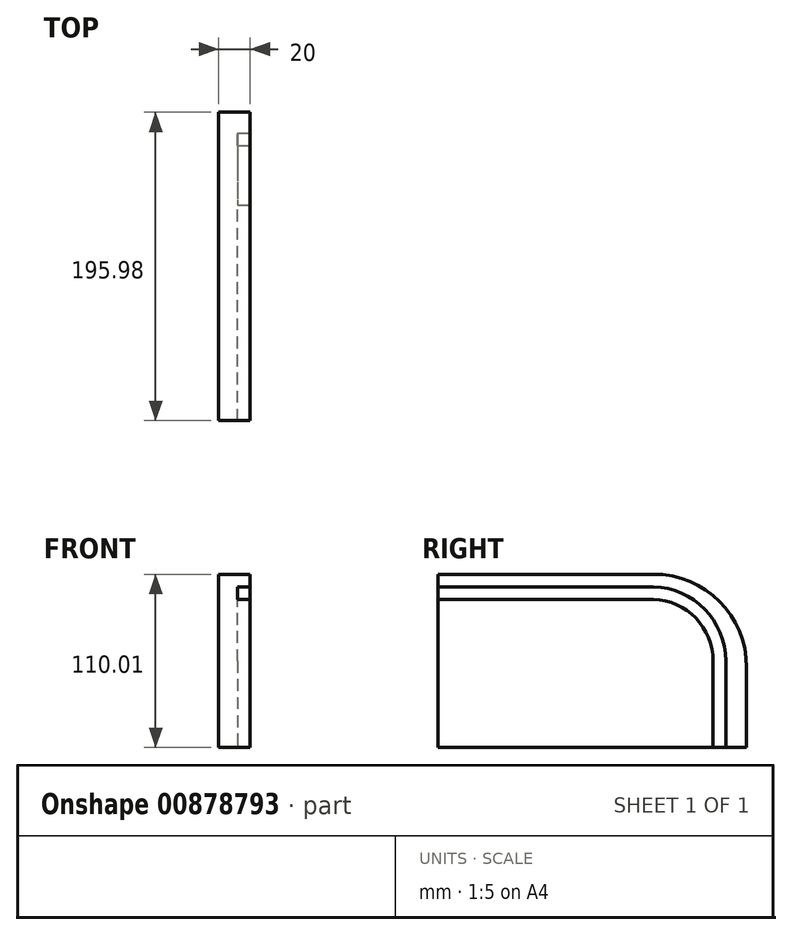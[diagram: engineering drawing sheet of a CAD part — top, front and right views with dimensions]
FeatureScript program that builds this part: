
annotation { "Feature Type Name" : "Feature", "Feature Type Description" : "" }
export const myFeature = defineFeature(function(context is Context, id is Id, definition is map)
    precondition{}
    {
        {
            var Q0;
            Q0=qCreatedBy(makeId("Right.planeOp"),FACE);
            var sketch = newSketch(context, id + "F0", { "sketchPlane" : qUnion([Q0])});
            skLineSegment(sketch, "E0.bottom", {"start": v(-98.14, 55.16) * mm, "end": v(97.84, 55.16) * mm});
            skLineSegment(sketch, "E0.top", {"start": v(-98.14, -54.85) * mm, "end": v(97.84, -54.85) * mm});
            skLineSegment(sketch, "E0.left", {"start": v(-98.14, 55.16) * mm, "end": v(-98.14, -54.85) * mm});
            skLineSegment(sketch, "E0.right", {"start": v(97.84, 55.16) * mm, "end": v(97.84, -54.85) * mm});
            skSolve(sketch);
        }
        {
            var Q0;
            Q0 = qSketchRegion(id + "F0", true);
            extrude(context, id + "F1", {"entities" : qUnion([Q0]), "oppositeDirection" : true, "depth" : 20 * mm, "offsetDistance" : 25 * mm});
        }
        {
            var Q0;
            Q0=makeQuery(id+"F1.opExtrude","SWEPT_EDGE",EDGE,{"disambiguationData":[OSD([sQuery(id+"F0.wireOp",EDGE,"E0.bottom"),sQuery(id+"F0.wireOp",EDGE,"E0.right")])]});
            fillet(context, id + "F2", {"entities" : qUnion([Q0]), "radius" : 59.15 * mm, "tangentPropagation" : true, "allowEdgeOverflow" : false});
        }
        {
            var Q0;
            Q0=makeQuery(id+"F1.opExtrude","CAP_FACE",FACE,{"disambiguationData":[OSD([sQuery(id+"F0.wireOp",EDGE,"E0.bottom"),sQuery(id+"F0.wireOp",EDGE,"E0.top"),sQuery(id+"F0.wireOp",EDGE,"E0.left"),sQuery(id+"F0.wireOp",EDGE,"E0.right")])],"isStart":true});
            var sketch = newSketch(context, id + "F3", { "sketchPlane" : qUnion([Q0])});
            skPoint(sketch, "E1", {"position": v(-98.14, 47.16) * mm});
            skPoint(sketch, "E2", {"position": v(38.69, 47.16) * mm});
            skPoint(sketch, "E3", {"position": v(84.57, -54.85) * mm});
            skPoint(sketch, "E4", {"position": v(84.57, 0) * mm});
            skLineSegment(sketch, "E5", {"start": v(-98.14, 47.16) * mm, "end": v(38.69, 47.16) * mm});
            skLineSegment(sketch, "E6", {"start": v(84.57, 0) * mm, "end": v(84.57, -54.85) * mm});
            skArc(sketch, "E7", {"start": v(84.57, 0) * mm, "mid": v(71.2, 32.9) * mm, "end": v(38.69, 47.16) * mm});
            skPoint(sketch, "E8", {"position": v(38.69, 39.16) * mm});
            skPoint(sketch, "E9", {"position": v(76.57, 0) * mm});
            skPoint(sketch, "E10", {"position": v(-98.14, 39.16) * mm});
            skLineSegment(sketch, "E11", {"start": v(-98.14, 39.16) * mm, "end": v(38.69, 39.16) * mm});
            skPoint(sketch, "E12", {"position": v(76.57, -54.85) * mm});
            skLineSegment(sketch, "E13", {"start": v(76.57, 0) * mm, "end": v(76.57, -54.85) * mm});
            skArc(sketch, "E14", {"start": v(76.57, 0) * mm, "mid": v(65.55, 27.24) * mm, "end": v(38.69, 39.16) * mm});
            skSolve(sketch);
        }
        {
            var Q0;
            {var subQ1=sQuery(id+"F3.wireOp",EDGE,"E5");Q0=makeQuery(id+"F3.imprint","IMPRINT",FACE,{"disambiguationData":[TD([[makeQuery(id+"F3.imprint","IMPRINT",EDGE,{"derivedFrom":subQ1}),-1.0]])]});}
            extrude(context, id + "F4", {"entities" : qUnion([Q0]), "operationType" : NewBodyOperationType.REMOVE, "oppositeDirection" : true, "depth" : 8 * mm, "offsetDistance" : 25 * mm});
        }
    });
